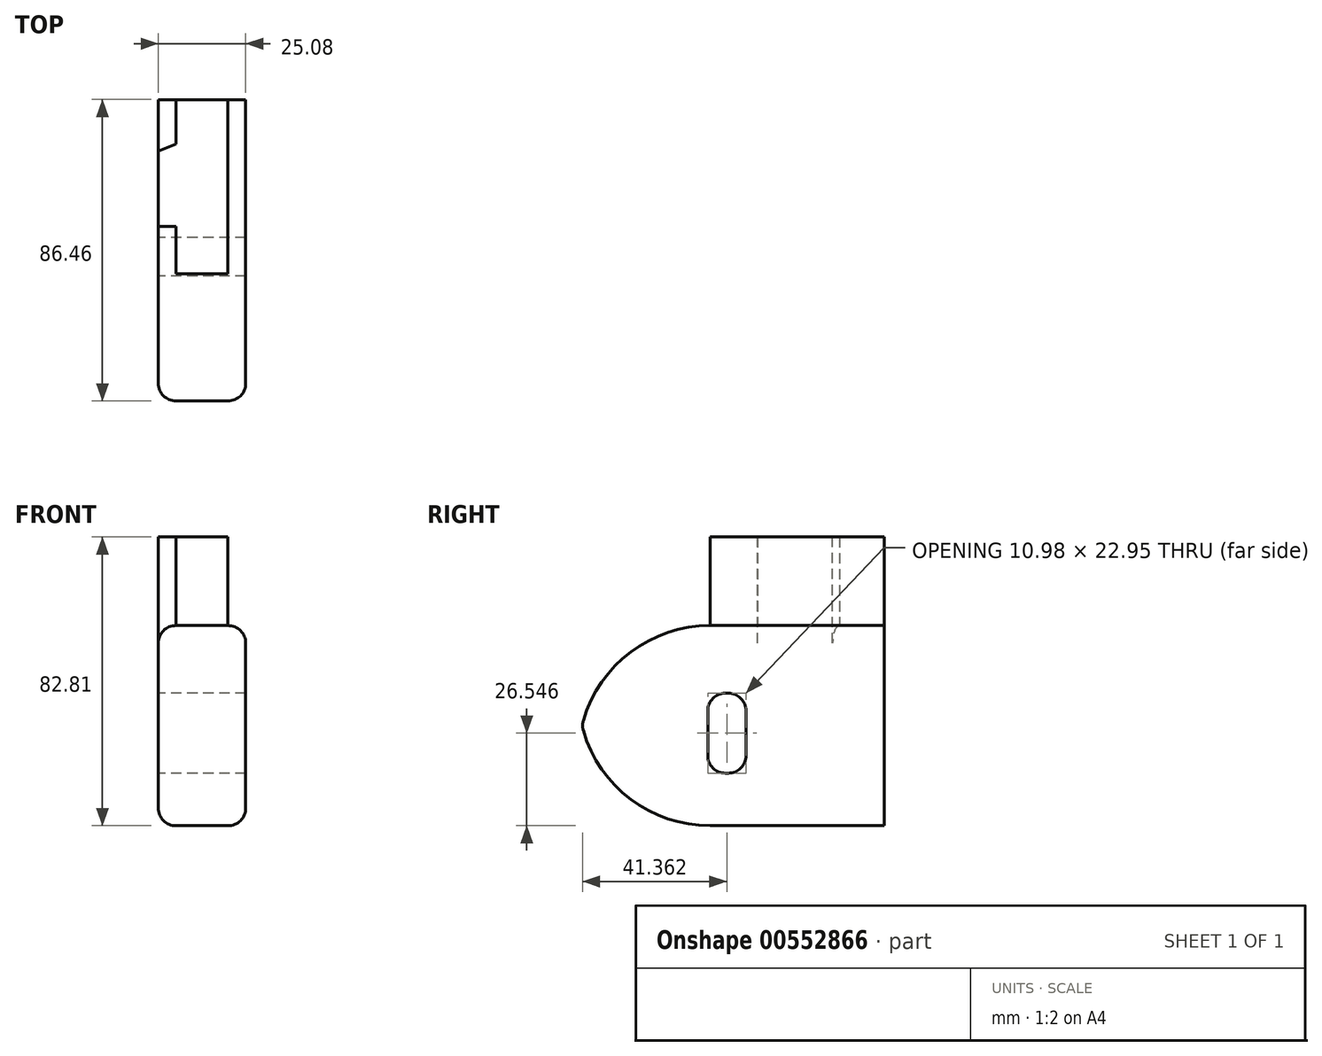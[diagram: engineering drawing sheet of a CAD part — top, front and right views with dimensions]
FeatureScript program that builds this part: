
annotation { "Feature Type Name" : "Feature", "Feature Type Description" : "" }
export const myFeature = defineFeature(function(context is Context, id is Id, definition is map)
    precondition{}
    {
        {
            var Q0;
            Q0=qCreatedBy(makeId("Top.planeOp"),FACE);
            var sketch = newSketch(context, id + "F0", { "sketchPlane" : qUnion([Q0])});
            skLineSegment(sketch, "E0.bottom", {"start": v(25.08, 54.66) * mm, "end": v(0, 54.66) * mm});
            skLineSegment(sketch, "E0.top", {"start": v(25.08, -33.1) * mm, "end": v(0, -33.1) * mm});
            skLineSegment(sketch, "E0.left", {"start": v(25.08, 54.66) * mm, "end": v(25.08, -33.1) * mm});
            skLineSegment(sketch, "E0.right", {"start": v(0, 54.66) * mm, "end": v(0, -33.1) * mm});
            skSolve(sketch);
        }
        {
            var Q0;
            Q0 = qSketchRegion(id + "F0", true);
            extrude(context, id + "F1", {"entities" : qUnion([Q0]), "depth" : 57.4 * mm, "offsetDistance" : 25.4 * mm});
        }
        {
            var Q0;
            Q0=makeQuery(id+"F1.opExtrude","CAP_EDGE",EDGE,{"disambiguationData":[OSD([sQuery(id+"F0.wireOp",EDGE,"E0.top")])],"isStart":false});
            var Q1;
            Q1=makeQuery(id+"F1.opExtrude","CAP_EDGE",EDGE,{"disambiguationData":[OSD([sQuery(id+"F0.wireOp",EDGE,"E0.top")])],"isStart":true});
            fillet(context, id + "F2", {"entities" : qUnion([Q0, Q1]), "radius" : 37.8 * mm, "tangentPropagation" : true, "allowEdgeOverflow" : false});
        }
        {
            var Q0;
            Q0=makeQuery(id+"F1.opExtrude","CAP_EDGE",EDGE,{"disambiguationData":[OSD([sQuery(id+"F0.wireOp",EDGE,"E0.right")])],"isStart":true});
            var Q1;
            Q1=makeQuery(id+"F2.opFillet","BLEND_EDGE",EDGE,{"blendedFrom":[makeQuery(id+"F1.opExtrude","CAP_EDGE",EDGE,{"disambiguationData":[OSD([sQuery(id+"F0.wireOp",EDGE,"E0.top")])],"isStart":true}),makeQuery(id+"F1.opExtrude","SWEPT_FACE",FACE,{"disambiguationData":[OSD([sQuery(id+"F0.wireOp",EDGE,"E0.right")])]})],"blendedInto":[makeQuery(id+"F1.opExtrude","SWEPT_FACE",FACE,{"disambiguationData":[OSD([sQuery(id+"F0.wireOp",EDGE,"E0.right")])]})]});
            var Q2;
            Q2=makeQuery(id+"F1.opExtrude","CAP_EDGE",EDGE,{"disambiguationData":[OSD([sQuery(id+"F0.wireOp",EDGE,"E0.left")])],"isStart":false});
            var Q3;
            Q3=makeQuery(id+"F2.opFillet","BLEND_EDGE",EDGE,{"blendedFrom":[makeQuery(id+"F1.opExtrude","CAP_EDGE",EDGE,{"disambiguationData":[OSD([sQuery(id+"F0.wireOp",EDGE,"E0.top")])],"isStart":false}),makeQuery(id+"F1.opExtrude","SWEPT_FACE",FACE,{"disambiguationData":[OSD([sQuery(id+"F0.wireOp",EDGE,"E0.left")])]})],"blendedInto":[makeQuery(id+"F1.opExtrude","SWEPT_FACE",FACE,{"disambiguationData":[OSD([sQuery(id+"F0.wireOp",EDGE,"E0.left")])]})]});
            var Q4;
            Q4=makeQuery(id+"F1.opExtrude","CAP_EDGE",EDGE,{"disambiguationData":[OSD([sQuery(id+"F0.wireOp",EDGE,"E0.left")])],"isStart":true});
            var Q5;
            Q5=makeQuery(id+"F2.opFillet","BLEND_EDGE",EDGE,{"blendedFrom":[makeQuery(id+"F1.opExtrude","CAP_EDGE",EDGE,{"disambiguationData":[OSD([sQuery(id+"F0.wireOp",EDGE,"E0.top")])],"isStart":true}),makeQuery(id+"F1.opExtrude","SWEPT_FACE",FACE,{"disambiguationData":[OSD([sQuery(id+"F0.wireOp",EDGE,"E0.left")])]})],"blendedInto":[makeQuery(id+"F1.opExtrude","SWEPT_FACE",FACE,{"disambiguationData":[OSD([sQuery(id+"F0.wireOp",EDGE,"E0.left")])]})]});
            var Q6;
            Q6=makeQuery(id+"F2.opFillet","BLEND_EDGE",EDGE,{"blendedFrom":[makeQuery(id+"F1.opExtrude","CAP_EDGE",EDGE,{"disambiguationData":[OSD([sQuery(id+"F0.wireOp",EDGE,"E0.top")])],"isStart":false}),makeQuery(id+"F1.opExtrude","SWEPT_FACE",FACE,{"disambiguationData":[OSD([sQuery(id+"F0.wireOp",EDGE,"E0.right")])]})],"blendedInto":[makeQuery(id+"F1.opExtrude","SWEPT_FACE",FACE,{"disambiguationData":[OSD([sQuery(id+"F0.wireOp",EDGE,"E0.right")])]})]});
            var Q7;
            Q7=makeQuery(id+"F1.opExtrude","CAP_EDGE",EDGE,{"disambiguationData":[OSD([sQuery(id+"F0.wireOp",EDGE,"E0.right")])],"isStart":false});
            fillet(context, id + "F3", {"entities" : qUnion([Q0, Q1, Q2, Q3, Q4, Q5, Q6, Q7]), "radius" : 5.08 * mm, "tangentPropagation" : true, "allowEdgeOverflow" : false});
        }
        {
            var Q0;
            {var subQ0=sQuery(id+"F0.wireOp",EDGE,"E0.top");Q0=makeQuery(id+"F2.opFillet","BLEND_EDGE",EDGE,{"blendedFrom":[makeQuery(id+"F1.opExtrude","CAP_EDGE",EDGE,{"disambiguationData":[OSD([subQ0])],"isStart":true}),makeQuery(id+"F1.opExtrude","CAP_EDGE",EDGE,{"disambiguationData":[OSD([subQ0])],"isStart":false})],"blendedInto":[]});}
            fillet(context, id + "F4", {"entities" : qUnion([Q0]), "radius" : 5.08 * mm, "tangentPropagation" : true, "allowEdgeOverflow" : false});
        }
        {
            var Q0;
            Q0=makeQuery(id+"F1.opExtrude","SWEPT_FACE",FACE,{"disambiguationData":[OSD([sQuery(id+"F0.wireOp",EDGE,"E0.right")])]});
            var sketch = newSketch(context, id + "F5", { "sketchPlane" : qUnion([Q0])});
            skLineSegment(sketch, "E1.bottom", {"start": v(-4.07, 15.07) * mm, "end": v(-15.05, 15.07) * mm});
            skLineSegment(sketch, "E1.top", {"start": v(-4.07, 38.02) * mm, "end": v(-15.05, 38.02) * mm});
            skLineSegment(sketch, "E1.left", {"start": v(-4.07, 15.07) * mm, "end": v(-4.07, 38.02) * mm});
            skLineSegment(sketch, "E1.right", {"start": v(-15.05, 15.07) * mm, "end": v(-15.05, 38.02) * mm});
            skPoint(sketch, "E1.middle", {"position": v(-9.56, 26.55) * mm});
            skSolve(sketch);
        }
        {
            var Q0;
            Q0=makeQuery(id+"F5.imprint","IMPRINT",FACE,{"disambiguationData":[TD([[makeQuery(id+"F5.imprint","IMPRINT",EDGE,{"derivedFrom":sQuery(id+"F5.wireOp",EDGE,"E1.bottom")}),-1.0]])]});
            extrude(context, id + "F6", {"entities" : qUnion([Q0]), "operationType" : NewBodyOperationType.REMOVE, "oppositeDirection" : true, "depth" : 76.76 * mm, "offsetDistance" : 25.4 * mm});
        }
        {
            var Q0;
            Q0=makeQuery(id+"F6.boolean.opBoolean","COPY",EDGE,{"derivedFrom":makeQuery(id+"F6.opExtrude","SWEPT_EDGE",EDGE,{"disambiguationData":[OSD([sQuery(id+"F5.wireOp",EDGE,"E1.top"),sQuery(id+"F5.wireOp",EDGE,"E1.left")])]})});
            var Q1;
            Q1=makeQuery(id+"F6.boolean.opBoolean","COPY",EDGE,{"derivedFrom":makeQuery(id+"F6.opExtrude","SWEPT_EDGE",EDGE,{"disambiguationData":[OSD([sQuery(id+"F5.wireOp",EDGE,"E1.bottom"),sQuery(id+"F5.wireOp",EDGE,"E1.left")])]})});
            var Q2;
            Q2=makeQuery(id+"F6.boolean.opBoolean","COPY",EDGE,{"derivedFrom":makeQuery(id+"F6.opExtrude","SWEPT_EDGE",EDGE,{"disambiguationData":[OSD([sQuery(id+"F5.wireOp",EDGE,"E1.bottom"),sQuery(id+"F5.wireOp",EDGE,"E1.right")])]})});
            var Q3;
            Q3=makeQuery(id+"F6.boolean.opBoolean","COPY",EDGE,{"derivedFrom":makeQuery(id+"F6.opExtrude","SWEPT_EDGE",EDGE,{"disambiguationData":[OSD([sQuery(id+"F5.wireOp",EDGE,"E1.top"),sQuery(id+"F5.wireOp",EDGE,"E1.right")])]})});
            fillet(context, id + "F7", {"entities" : qUnion([Q0, Q1, Q2, Q3]), "radius" : 5.08 * mm, "tangentPropagation" : true, "allowEdgeOverflow" : false});
        }
        {
            var Q0;
            Q0=makeQuery(id+"F1.opExtrude","CAP_FACE",FACE,{"disambiguationData":[OSD([sQuery(id+"F0.wireOp",EDGE,"E0.bottom"),sQuery(id+"F0.wireOp",EDGE,"E0.top"),sQuery(id+"F0.wireOp",EDGE,"E0.left"),sQuery(id+"F0.wireOp",EDGE,"E0.right")])],"isStart":false});
            var sketch = newSketch(context, id + "F8", { "sketchPlane" : qUnion([Q0])});
            skLineSegment(sketch, "E2", {"start": v(15.51, 18.31) * mm, "end": v(0, 18.31) * mm});
            skLineSegment(sketch, "E3", {"start": v(0, 18.31) * mm, "end": v(0, 39.87) * mm});
            skLineSegment(sketch, "E4", {"start": v(0, 39.87) * mm, "end": v(14.6, 45.62) * mm});
            skLineSegment(sketch, "E5", {"start": v(14.6, 45.62) * mm, "end": v(15.51, 18.31) * mm});
            skSolve(sketch);
        }
        {
            var Q0;
            {var subQ0=sQuery(id+"F8.wireOp",EDGE,"E3");Q0=makeQuery(id+"F8.imprint","IMPRINT",FACE,{"disambiguationData":[TD([[makeQuery(id+"F8.imprint","IMPRINT",EDGE,{"derivedFrom":subQ0}),-1.0]])]});}
            extrude(context, id + "F9", {"entities" : qUnion([Q0]), "operationType" : NewBodyOperationType.ADD, "oppositeDirection" : true, "depth" : 36.45 * mm, "offsetDistance" : 25.4 * mm});
        }
        {
            var Q0;
            {var subQ0=sQuery(id+"F0.wireOp",EDGE,"E0.right");var subQ1=sQuery(id+"F0.wireOp",EDGE,"E0.left");var subQ2=sQuery(id+"F0.wireOp",EDGE,"E0.top");var subQ3=sQuery(id+"F0.wireOp",EDGE,"E0.bottom");Q0=makeQuery(id+"F9.boolean.opBoolean","MERGE",FACE,{"derivedFrom":[makeQuery(id+"F1.opExtrude","CAP_FACE",FACE,{"disambiguationData":[OSD([subQ3,subQ2,subQ1,subQ0])],"isStart":false}),makeQuery(id+"F9.opExtrude","CAP_FACE",FACE,{"disambiguationData":[OSD([subQ3,subQ2,subQ1,subQ0,sQuery(id+"F8.wireOp",EDGE,"E2"),sQuery(id+"F8.wireOp",EDGE,"E3"),sQuery(id+"F8.wireOp",EDGE,"E4")])],"isStart":true})]});}
            extrude(context, id + "F10", {"entities" : qUnion([Q0]), "operationType" : NewBodyOperationType.ADD, "depth" : 25.4 * mm, "offsetDistance" : 25.4 * mm});
        }
    });
